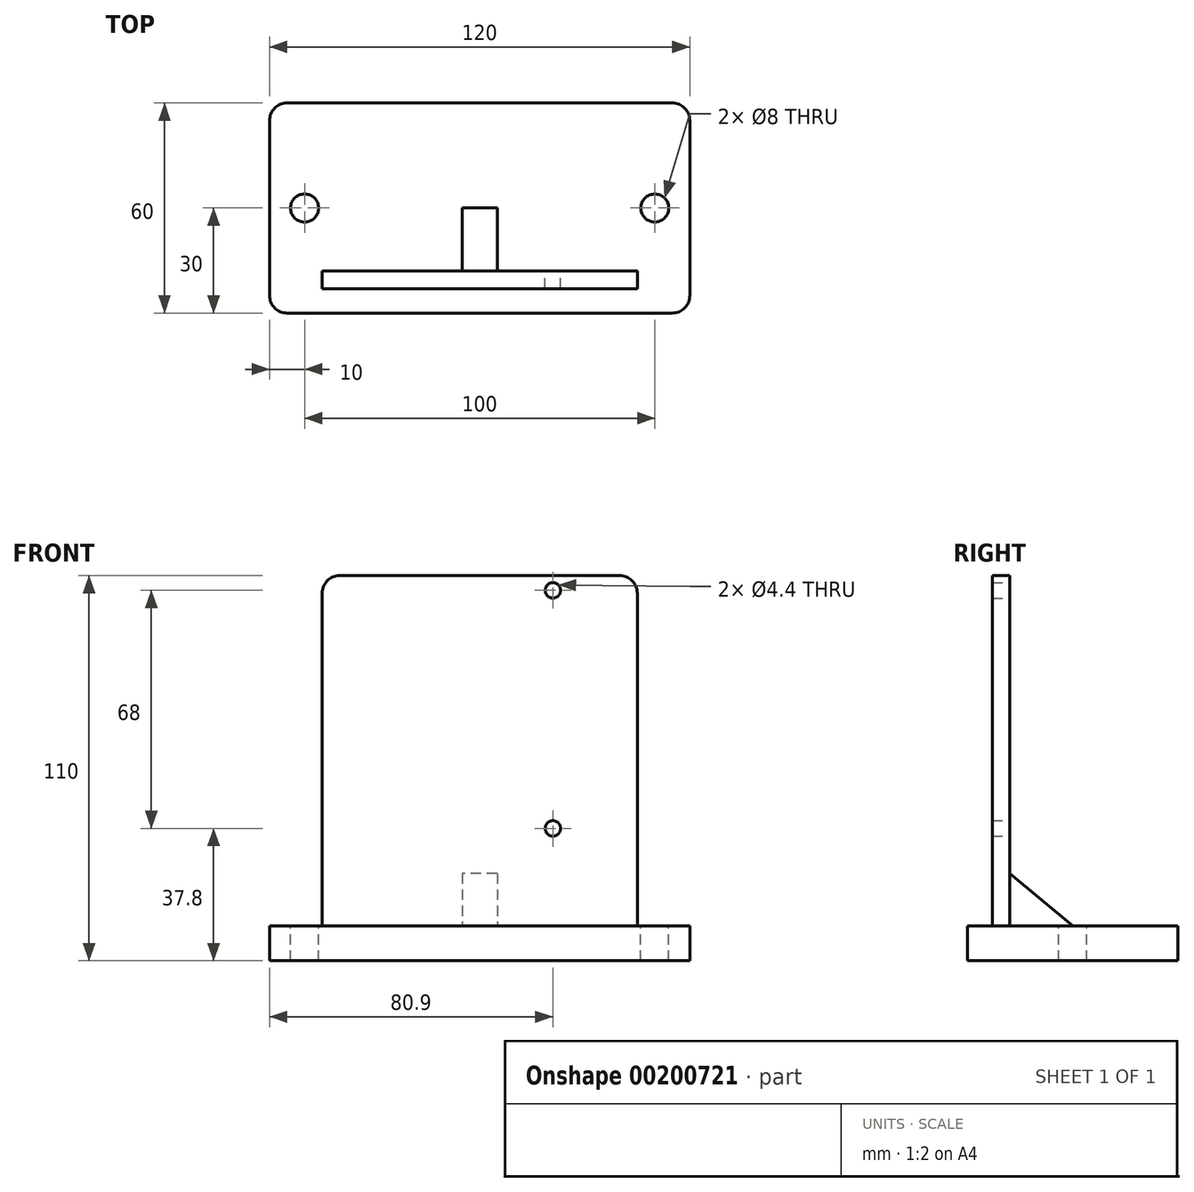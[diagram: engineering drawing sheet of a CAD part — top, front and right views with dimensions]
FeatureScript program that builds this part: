
annotation { "Feature Type Name" : "Feature", "Feature Type Description" : "" }
export const myFeature = defineFeature(function(context is Context, id is Id, definition is map)
    precondition{}
    {
        {
            var Q0;
            Q0=qCreatedBy(makeId("Top.planeOp"),FACE);
            var sketch = newSketch(context, id + "F0", { "sketchPlane" : qUnion([Q0])});
            skLineSegment(sketch, "E0.bottom", {"start": v(-60, 30) * mm, "end": v(60, 30) * mm});
            skLineSegment(sketch, "E0.top", {"start": v(-60, -30) * mm, "end": v(60, -30) * mm});
            skLineSegment(sketch, "E0.left", {"start": v(-60, 30) * mm, "end": v(-60, -30) * mm});
            skLineSegment(sketch, "E0.right", {"start": v(60, 30) * mm, "end": v(60, -30) * mm});
            skLineSegment(sketch, "E1", {"start": v(-60, 0) * mm, "end": v(60, 0) * mm, "construction": true});
            skCircle(sketch, "E2", {"center": v(-50, 0) * mm, "radius": 4 * mm});
            skLineSegment(sketch, "E3", {"start": v(0, 30) * mm, "end": v(0, -30) * mm, "construction": true});
            skCircle(sketch, "E4.MirrorC", {"center": v(50, 0) * mm, "radius": 4 * mm});
            skLineSegment(sketch, "E5.bottom", {"start": v(-41.1, 18) * mm, "end": v(41.1, 18) * mm, "construction": true});
            skLineSegment(sketch, "E5.top", {"start": v(-41.1, -18) * mm, "end": v(41.1, -18) * mm, "construction": true});
            skLineSegment(sketch, "E5.left", {"start": v(-41.1, 18) * mm, "end": v(-41.1, -18) * mm, "construction": true});
            skLineSegment(sketch, "E5.right", {"start": v(41.1, 18) * mm, "end": v(41.1, -18) * mm, "construction": true});
            skLineSegment(sketch, "E6", {"start": v(0, 18) * mm, "end": v(0, -18) * mm, "construction": true});
            skLineSegment(sketch, "E7", {"start": v(-41.1, 0) * mm, "end": v(41.1, 0) * mm, "construction": true});
            skSolve(sketch);
        }
        {
            var Q0;
            Q0=makeQuery(id+"F0.imprint","IMPRINT",FACE,{"disambiguationData":[TD([[makeQuery(id+"F0.imprint","IMPRINT",EDGE,{"derivedFrom":sQuery(id+"F0.wireOp",EDGE,"E0.bottom")}),-1.0]])]});
            extrude(context, id + "F1", {"entities" : qUnion([Q0]), "oppositeDirection" : true, "depth" : 10 * mm});
        }
        {
            var Q0;
            Q0=qCreatedBy(makeId("Front.planeOp"),FACE);
            cPlane(context, id + "F2", {"entities" : qUnion([Q0]), "cplaneType" : CPlaneType.OFFSET, "offset" : 18 * mm, "width" : 150 * mm, "height" : 150 * mm});
        }
        {
            var Q0;
            Q0=qCreatedBy(id+"F2.planeOp",FACE);
            var sketch = newSketch(context, id + "F3", { "sketchPlane" : qUnion([Q0])});
            skLineSegment(sketch, "E8.bottom", {"start": v(-45, 100) * mm, "end": v(45, 100) * mm});
            skLineSegment(sketch, "E8.top", {"start": v(-45, -10) * mm, "end": v(45, -10) * mm});
            skLineSegment(sketch, "E8.left", {"start": v(-45, 100) * mm, "end": v(-45, -10) * mm});
            skLineSegment(sketch, "E8.right", {"start": v(45, 100) * mm, "end": v(45, -10) * mm});
            skLineSegment(sketch, "E9.0", {"start": v(-60, -10) * mm, "end": v(60, -10) * mm, "construction": true});
            skLineSegment(sketch, "E10", {"start": v(0, 100) * mm, "end": v(0, -10) * mm, "construction": true});
            skLineSegment(sketch, "E11.bottom", {"start": v(-41.1, 100) * mm, "end": v(41.1, 100) * mm, "construction": true});
            skLineSegment(sketch, "E11.top", {"start": v(-41.1, 23.8) * mm, "end": v(41.1, 23.8) * mm, "construction": true});
            skLineSegment(sketch, "E11.left", {"start": v(-41.1, 100) * mm, "end": v(-41.1, 23.8) * mm, "construction": true});
            skLineSegment(sketch, "E11.right", {"start": v(41.1, 100) * mm, "end": v(41.1, 23.8) * mm, "construction": true});
            skLineSegment(sketch, "E12.0", {"start": v(-45, 0) * mm, "end": v(45, 0) * mm});
            skLineSegment(sketch, "E13.0", {"start": v(-60, -10) * mm, "end": v(-60, 0) * mm, "construction": true});
            skPoint(sketch, "E14.orphan", {"position": v(-60, 0) * mm});
            skPoint(sketch, "E15.orphan", {"position": v(60, 0) * mm});
            skLineSegment(sketch, "E16", {"start": v(20.9, 100) * mm, "end": v(20.9, 23.8) * mm, "construction": true});
            skCircle(sketch, "E17", {"center": v(20.9, 95.8) * mm, "radius": 2.2 * mm, "construction": true});
            skCircle(sketch, "E18", {"center": v(20.9, 27.8) * mm, "radius": 2.2 * mm, "construction": true});
            skSolve(sketch);
        }
        {
            var Q0;
            {var subQ0=sQuery(id+"F3.wireOp",EDGE,"E8.bottom");Q0=makeQuery(id+"F3.imprint","IMPRINT",FACE,{"disambiguationData":[TD([[makeQuery(id+"F3.imprint","IMPRINT",EDGE,{"derivedFrom":subQ0}),-1.0]])]});}
            extrude(context, id + "F4", {"entities" : qUnion([Q0]), "operationType" : NewBodyOperationType.ADD, "depth" : 5 * mm});
        }
        {
            var Q0;
            Q0=sQuery(id+"F0.wireOp",VERTEX,"E2.center");
            var Q1;
            Q1=makeQuery(id+"F1.opExtrude","SWEPT_BODY",BODY,{"disambiguationData":[OSD([sQuery(id+"F0.wireOp",EDGE,"E0.bottom"),sQuery(id+"F0.wireOp",EDGE,"E0.top"),sQuery(id+"F0.wireOp",EDGE,"E0.left"),sQuery(id+"F0.wireOp",EDGE,"E0.right")])]});
            hole(context, id + "F5", {"style" : HoleStyle.SIMPLE, "endStyle" : HoleEndStyle.THROUGH, "holeDiameter" : 8 * mm, "locations" : qUnion([Q0]), "scope" : qUnion([Q1]), "isTappedThrough" : true});
        }
        {
            var Q0;
            Q0=sQuery(id+"F0.wireOp",VERTEX,"E4.MirrorC.center");
            var Q1;
            Q1=makeQuery(id+"F1.opExtrude","SWEPT_BODY",BODY,{"disambiguationData":[OSD([sQuery(id+"F0.wireOp",EDGE,"E0.bottom"),sQuery(id+"F0.wireOp",EDGE,"E0.top"),sQuery(id+"F0.wireOp",EDGE,"E0.left"),sQuery(id+"F0.wireOp",EDGE,"E0.right")])]});
            hole(context, id + "F6", {"style" : HoleStyle.SIMPLE, "endStyle" : HoleEndStyle.THROUGH, "holeDiameter" : 8 * mm, "locations" : qUnion([Q0]), "scope" : qUnion([Q1]), "isTappedThrough" : true});
        }
        {
            var Q0;
            Q0=sQuery(id+"F3.wireOp",VERTEX,"E17.center");
            var Q1;
            Q1=makeQuery(id+"F1.opExtrude","SWEPT_BODY",BODY,{"disambiguationData":[OSD([sQuery(id+"F0.wireOp",EDGE,"E0.bottom"),sQuery(id+"F0.wireOp",EDGE,"E0.top"),sQuery(id+"F0.wireOp",EDGE,"E0.left"),sQuery(id+"F0.wireOp",EDGE,"E0.right")])]});
            hole(context, id + "F7", {"style" : HoleStyle.SIMPLE, "endStyle" : HoleEndStyle.THROUGH, "oppositeDirection" : true, "holeDiameter" : 4.4 * mm, "locations" : qUnion([Q0]), "scope" : qUnion([Q1]), "isTappedThrough" : true});
        }
        {
            var Q0;
            Q0=sQuery(id+"F3.wireOp",VERTEX,"E18.center");
            var Q1;
            Q1=makeQuery(id+"F1.opExtrude","SWEPT_BODY",BODY,{"disambiguationData":[OSD([sQuery(id+"F0.wireOp",EDGE,"E0.bottom"),sQuery(id+"F0.wireOp",EDGE,"E0.top"),sQuery(id+"F0.wireOp",EDGE,"E0.left"),sQuery(id+"F0.wireOp",EDGE,"E0.right")])]});
            hole(context, id + "F8", {"style" : HoleStyle.SIMPLE, "endStyle" : HoleEndStyle.THROUGH, "oppositeDirection" : true, "holeDiameter" : 4.4 * mm, "locations" : qUnion([Q0]), "scope" : qUnion([Q1]), "isTappedThrough" : true});
        }
        {
            var Q0;
            Q0=makeQuery(id+"F1.opExtrude","SWEPT_EDGE",EDGE,{"disambiguationData":[OSD([sQuery(id+"F0.wireOp",EDGE,"E0.top"),sQuery(id+"F0.wireOp",EDGE,"E0.left")])]});
            fillet(context, id + "F9", {"entities" : qUnion([Q0]), "radius" : 5 * mm, "tangentPropagation" : true, "allowEdgeOverflow" : false});
        }
        {
            var Q0;
            Q0=makeQuery(id+"F1.opExtrude","SWEPT_EDGE",EDGE,{"disambiguationData":[OSD([sQuery(id+"F0.wireOp",EDGE,"E0.bottom"),sQuery(id+"F0.wireOp",EDGE,"E0.left")])]});
            fillet(context, id + "F10", {"entities" : qUnion([Q0]), "radius" : 5 * mm, "tangentPropagation" : true, "allowEdgeOverflow" : false});
        }
        {
            var Q0;
            Q0=makeQuery(id+"F1.opExtrude","SWEPT_EDGE",EDGE,{"disambiguationData":[OSD([sQuery(id+"F0.wireOp",EDGE,"E0.bottom"),sQuery(id+"F0.wireOp",EDGE,"E0.right")])]});
            fillet(context, id + "F11", {"entities" : qUnion([Q0]), "radius" : 5 * mm, "tangentPropagation" : true, "allowEdgeOverflow" : false});
        }
        {
            var Q0;
            Q0=makeQuery(id+"F1.opExtrude","SWEPT_EDGE",EDGE,{"disambiguationData":[OSD([sQuery(id+"F0.wireOp",EDGE,"E0.top"),sQuery(id+"F0.wireOp",EDGE,"E0.right")])]});
            fillet(context, id + "F12", {"entities" : qUnion([Q0]), "radius" : 5 * mm, "tangentPropagation" : true, "allowEdgeOverflow" : false});
        }
        {
            var Q0;
            Q0=makeQuery(id+"F4.opExtrude","SWEPT_EDGE",EDGE,{"disambiguationData":[OSD([sQuery(id+"F3.wireOp",EDGE,"E8.bottom"),sQuery(id+"F3.wireOp",EDGE,"E8.right")])]});
            fillet(context, id + "F13", {"entities" : qUnion([Q0]), "radius" : 5 * mm, "tangentPropagation" : true, "allowEdgeOverflow" : false});
        }
        {
            var Q0;
            Q0=makeQuery(id+"F4.opExtrude","SWEPT_EDGE",EDGE,{"disambiguationData":[OSD([sQuery(id+"F3.wireOp",EDGE,"E8.bottom"),sQuery(id+"F3.wireOp",EDGE,"E8.left")])]});
            fillet(context, id + "F14", {"entities" : qUnion([Q0]), "radius" : 5 * mm, "tangentPropagation" : true, "allowEdgeOverflow" : false});
        }
        {
            var Q0;
            Q0=qCreatedBy(makeId("Right.planeOp"),FACE);
            var sketch = newSketch(context, id + "F15", { "sketchPlane" : qUnion([Q0])});
            skLineSegment(sketch, "E19.0", {"start": v(-18, 15) * mm, "end": v(-18, 0) * mm});
            skLineSegment(sketch, "E20.0", {"start": v(0, 0) * mm, "end": v(-18, 0) * mm});
            skPoint(sketch, "E21.orphan", {"position": v(-30, 0) * mm});
            skPoint(sketch, "E22.orphan", {"position": v(-18, -10) * mm});
            skLineSegment(sketch, "E23", {"start": v(-18, 15) * mm, "end": v(0, 0) * mm});
            skPoint(sketch, "E24.orphan", {"position": v(-18, 100) * mm});
            skPoint(sketch, "E25.orphan", {"position": v(30, 0) * mm});
            skLineSegment(sketch, "E26.0", {"start": v(-23, 95) * mm, "end": v(-23, 0) * mm});
            skSolve(sketch);
        }
        {
            var Q0;
            Q0=makeQuery(id+"F15.imprint","IMPRINT",FACE,{"disambiguationData":[TD([[makeQuery(id+"F15.imprint","IMPRINT",EDGE,{"derivedFrom":sQuery(id+"F15.wireOp",EDGE,"E19.0")}),1.0]])]});
            extrude(context, id + "F16", {"entities" : qUnion([Q0]), "operationType" : NewBodyOperationType.ADD, "endBound" : BoundingType.SYMMETRIC, "depth" : 10 * mm});
        }
    });
